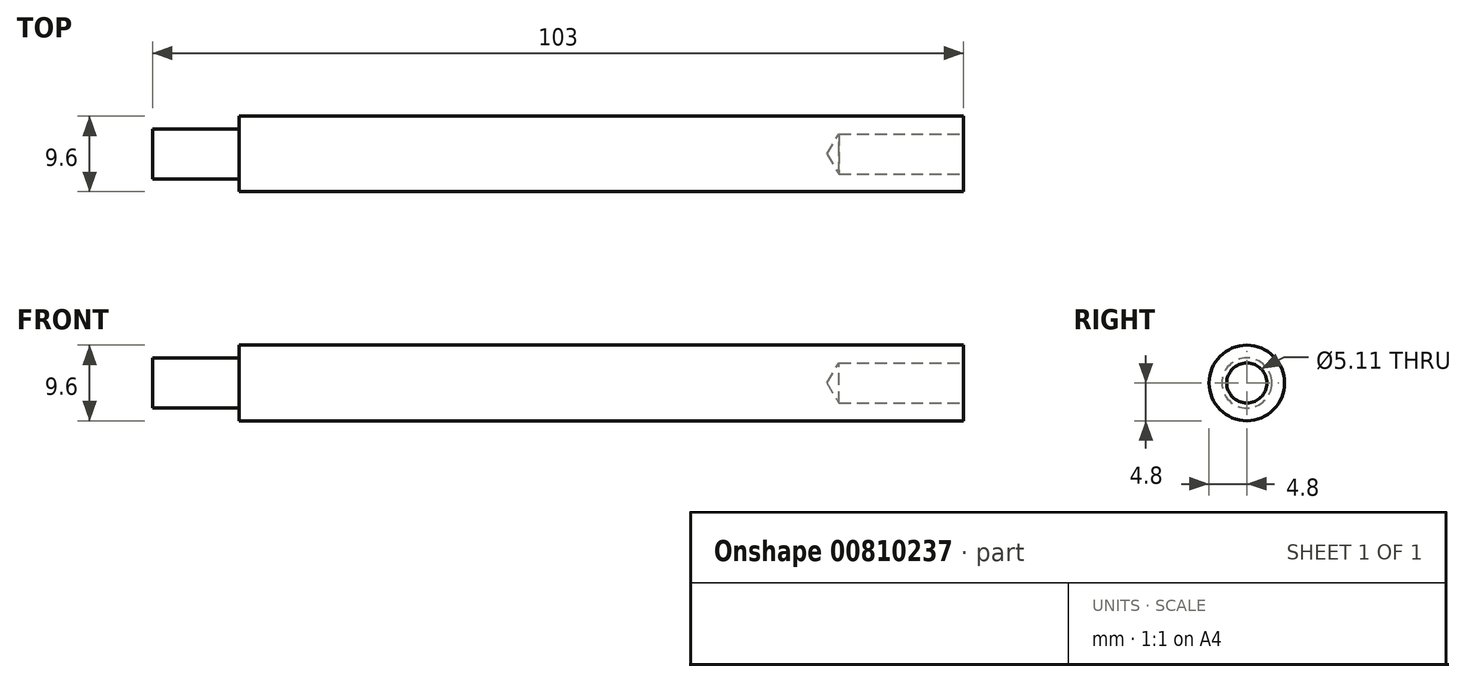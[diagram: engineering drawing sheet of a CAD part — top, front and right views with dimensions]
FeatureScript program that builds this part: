
annotation { "Feature Type Name" : "Feature", "Feature Type Description" : "" }
export const myFeature = defineFeature(function(context is Context, id is Id, definition is map)
    precondition{}
    {
        {
            var Q0;
            Q0=qCreatedBy(makeId("Right.planeOp"),FACE);
            var sketch = newSketch(context, id + "F0", { "sketchPlane" : qUnion([Q0])});
            skCircle(sketch, "E0", {"center": v(0, 0) * mm, "radius": 4.8 * mm});
            skSolve(sketch);
        }
        {
            var Q0;
            Q0 = qSketchRegion(id + "F0", true);
            extrude(context, id + "F1", {"entities" : qUnion([Q0]), "endBound" : BoundingType.SYMMETRIC, "depth" : 92 * mm, "offsetDistance" : 25 * mm});
        }
        {
            var Q0;
            Q0=makeQuery(id+"F1.opExtrude","CAP_FACE",FACE,{"disambiguationData":[OSD([sQuery(id+"F0.wireOp",EDGE,"E0")])],"isStart":false});
            var sketch = newSketch(context, id + "F2", { "sketchPlane" : qUnion([Q0])});
            skPoint(sketch, "E1", {"position": v(0, 0) * mm});
            skSolve(sketch);
        }
        {
            var Q0;
            Q0=sQuery(id+"F2.wireOp",VERTEX,"E1");
            var Q1;
            Q1=makeQuery(id+"F1.opExtrude","SWEPT_BODY",BODY,{"disambiguationData":[OSD([sQuery(id+"F0.wireOp",EDGE,"E0")])]});
            hole(context, id + "F3", {"style" : HoleStyle.SIMPLE, "endStyle" : HoleEndStyle.BLIND, "standardTappedOrClearance" : lookupTablePath({ "standard" : "ANSI", "engagement" : "75%", "pitch" : "20 tpi", "size" : "1/4", "type" : "Tapped" }), "standardBlindInLast" : lookupTablePath({ "standard" : "ANSI", "engagement" : "75%", "pitch" : "20 tpi", "size" : "1/4", "type" : "Tapped" }), "holeDiameter" : 5.1 * mm, "majorDiameter" : 6.35 * mm, "showTappedDepth" : true, "holeDepth" : 15.8 * mm, "isTappedThrough" : true, "tappedDepth" : 12 * mm, "tapClearance" : 3, "locations" : qUnion([Q0]), "scope" : qUnion([Q1])});
        }
        {
            var Q0;
            Q0=makeQuery(id+"F1.opExtrude","CAP_FACE",FACE,{"disambiguationData":[OSD([sQuery(id+"F0.wireOp",EDGE,"E0")])],"isStart":true});
            var sketch = newSketch(context, id + "F4", { "sketchPlane" : qUnion([Q0])});
            skCircle(sketch, "E2", {"center": v(0, 0) * mm, "radius": 3.17 * mm});
            skSolve(sketch);
        }
        {
            var Q0;
            Q0 = qSketchRegion(id + "F4", true);
            extrude(context, id + "F5", {"entities" : qUnion([Q0]), "operationType" : NewBodyOperationType.ADD, "depth" : 11 * mm, "offsetDistance" : 25 * mm});
        }
    });
